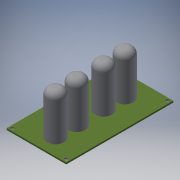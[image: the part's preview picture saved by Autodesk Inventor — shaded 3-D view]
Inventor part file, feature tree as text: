
AUTODESK INVENTOR PART (.ipt)
format: ipt  version: 2017 (Build 210142000, 142)  size: 177,152 bytes
history: native  units: in
note: dims shown in document units (in); Inventor stores cm internally (conversion verified against a paired STEP export)
features: extrude x4, sketch x4, fillet x1, projected_geometry x1
ambient origin geometry x8: Origin, YZ Plane, XZ Plane, XY Plane, X Axis, Y Axis, Z Axis, Center Point
bodies: Body1 (feature_tree)
feature tree (10):
  extrude  "Extrusion4"  Depth=4.4in
  extrude  "Extrusion5"  Depth=0.062in
  extrude  "Extrusion6"  Depth=0.1359in
  fillet  "Fillet2"  Radius=0.1359in
  extrude  "Extrusion7"  Depth=1.8in
  sketch  "Sketch3"  dims[d53=2.45in d54=4.4in]
  sketch  "Sketch4"  dims[d55=0.062in d56=0.0in d57=0.1359in]
  projected_geometry  "Projected Loop1"
  sketch  "Sketch5"  dims[d58=0.1359in d59=0.1359in d60=0.1359in d61=0.125in]
  sketch  "Sketch6"  dims[d62=0.125in d63=0.125in d64=0.125in d65=0.125in d66=0.125in d67=0.125in d68=0.125in d69=0.1in d70=0.0in d71=0.705in d72=0.705in d73=0.705in d74=0.705in d75=0.68in d78=0.87in d80=1.1in d82=0.87in d83=1.8in d84=0.0in d85=0.25in d86=1.33in d87=1.68in d88=0.08in d89=0.9in d90=1.8in d91=0.0in]
